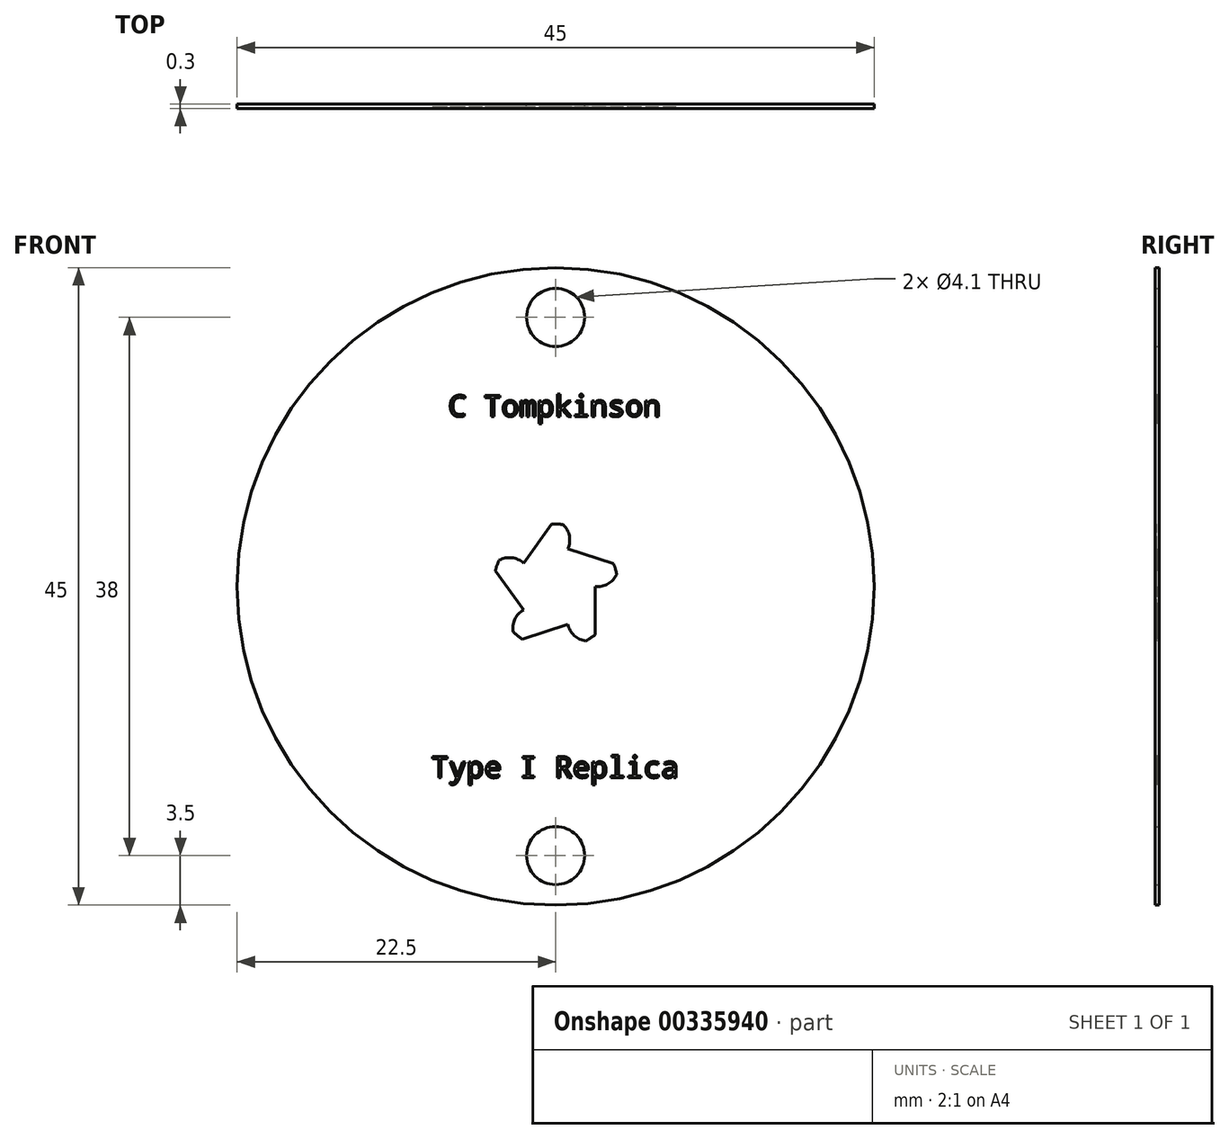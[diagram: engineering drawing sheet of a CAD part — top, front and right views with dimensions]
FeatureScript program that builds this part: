
annotation { "Feature Type Name" : "Feature", "Feature Type Description" : "" }
export const myFeature = defineFeature(function(context is Context, id is Id, definition is map)
    precondition{}
    {
        {
            var Q0;
            Q0=qCreatedBy(makeId("Front.planeOp"),FACE);
            var sketch = newSketch(context, id + "F0", { "sketchPlane" : qUnion([Q0])});
            skCircle(sketch, "E0", {"center": v(0, 0) * mm, "radius": 22.5 * mm});
            skCircle(sketch, "E1", {"center": v(0, 0) * mm, "radius": 19 * mm, "construction": true});
            skCircle(sketch, "E2", {"center": v(0, 19) * mm, "radius": 2.05 * mm});
            skCircle(sketch, "E3", {"center": v(0, -19) * mm, "radius": 2.05 * mm});
            skSolve(sketch);
        }
        {
            var Q0;
            Q0 = qSketchRegion(id + "F0", true);
            extrude(context, id + "F1", {"entities" : qUnion([Q0]), "depth" : 0.3 * mm});
        }
        {
            var Q0;
            Q0=makeQuery(id+"F1.opExtrude","CAP_FACE",FACE,{"disambiguationData":[OSD([sQuery(id+"F0.wireOp",EDGE,"E0"),sQuery(id+"F0.wireOp",EDGE,"E2"),sQuery(id+"F0.wireOp",EDGE,"E3")])],"isStart":false});
            var sketch = newSketch(context, id + "F2", { "sketchPlane" : qUnion([Q0])});
            skText(sketch, "E4", { "text": "Type I Replica", "fontName": "DroidSansMono.ttf"});
            skPoint(sketch, "E5", {"position": v(0, -12) * mm});
            skCircle(sketch, "E6", {"center": v(0, 0) * mm, "radius": 4.4 * mm, "construction": true});
            skCircle(sketch, "E7", {"center": v(0, 0) * mm, "radius": 3.3 * mm, "construction": true});
            skCircle(sketch, "E8", {"center": v(0, 0) * mm, "radius": 2.8 * mm, "construction": true});
            skLineSegment(sketch, "E9", {"start": v(2.8, 0) * mm, "end": v(2.8, -3.4) * mm});
            skArc(sketch, "E10", {"start": v(2.8, -3.4) * mm, "mid": v(2.48, -3.63) * mm, "end": v(2.14, -3.84) * mm});
            skArc(sketch, "E11", {"start": v(2.14, -3.84) * mm, "mid": v(1.31, -3.46) * mm, "end": v(0.87, -2.66) * mm});
            skLineSegment(sketch, "E12", {"start": v(0, 0) * mm, "end": v(0.87, -2.66) * mm, "construction": true});
            skLineSegment(sketch, "E13.1.0", {"start": v(0.87, 2.66) * mm, "end": v(4.1, 1.61) * mm});
            skArc(sketch, "E13.1.1", {"start": v(4.32, 0.85) * mm, "mid": v(3.7, 0.18) * mm, "end": v(2.8, 0) * mm});
            skLineSegment(sketch, "E13.2.0", {"start": v(-2.27, 1.65) * mm, "end": v(-0.27, 4.4) * mm});
            skArc(sketch, "E13.2.1", {"start": v(0.53, 4.37) * mm, "mid": v(0.97, 3.57) * mm, "end": v(0.87, 2.66) * mm});
            skLineSegment(sketch, "E13.3.0", {"start": v(-2.27, -1.65) * mm, "end": v(-4.26, 1.1) * mm});
            skArc(sketch, "E13.3.1", {"start": v(-4, 1.85) * mm, "mid": v(-3.1, 2.02) * mm, "end": v(-2.27, 1.65) * mm});
            skLineSegment(sketch, "E13.4.0", {"start": v(0.87, -2.66) * mm, "end": v(-2.36, -3.71) * mm});
            skArc(sketch, "E13.4.1", {"start": v(-3, -3.22) * mm, "mid": v(-2.88, -2.32) * mm, "end": v(-2.27, -1.65) * mm});
            skArc(sketch, "E14", {"start": v(-2.36, -3.71) * mm, "mid": v(-2.7, -3.48) * mm, "end": v(-3, -3.22) * mm});
            skArc(sketch, "E15", {"start": v(-4.26, 1.1) * mm, "mid": v(-4.14, 1.48) * mm, "end": v(-4, 1.85) * mm});
            skArc(sketch, "E16", {"start": v(-0.27, 4.4) * mm, "mid": v(0.13, 4.4) * mm, "end": v(0.53, 4.37) * mm});
            skText(sketch, "E17", { "text": "C Tompkinson", "fontName": "DroidSansMono.ttf"});
            skPoint(sketch, "E18.orphan", {"position": v(0.87, 2.66) * mm});
            skPoint(sketch, "E19.orphan", {"position": v(-2.27, 1.65) * mm});
            skPoint(sketch, "E20.orphan", {"position": v(2.8, 0) * mm});
            skArc(sketch, "E21", {"start": v(4.1, 1.61) * mm, "mid": v(4.22, 1.24) * mm, "end": v(4.32, 0.85) * mm});
            const initialGuessF2  = {"E4": [-0.0088, -0.0135, 1, 0, 0.0015], "E17": [-0.00758, 0.012, 1, 0, 0.0015]};
            skSetInitialGuess(sketch, initialGuessF2);
            skSolve(sketch);
        }
        {
            var Q0;
            Q0 = qSketchRegion(id + "F2", true);
            extrude(context, id + "F3", {"entities" : qUnion([Q0]), "operationType" : NewBodyOperationType.REMOVE, "oppositeDirection" : true, "depth" : 0.1 * mm});
        }
    });
